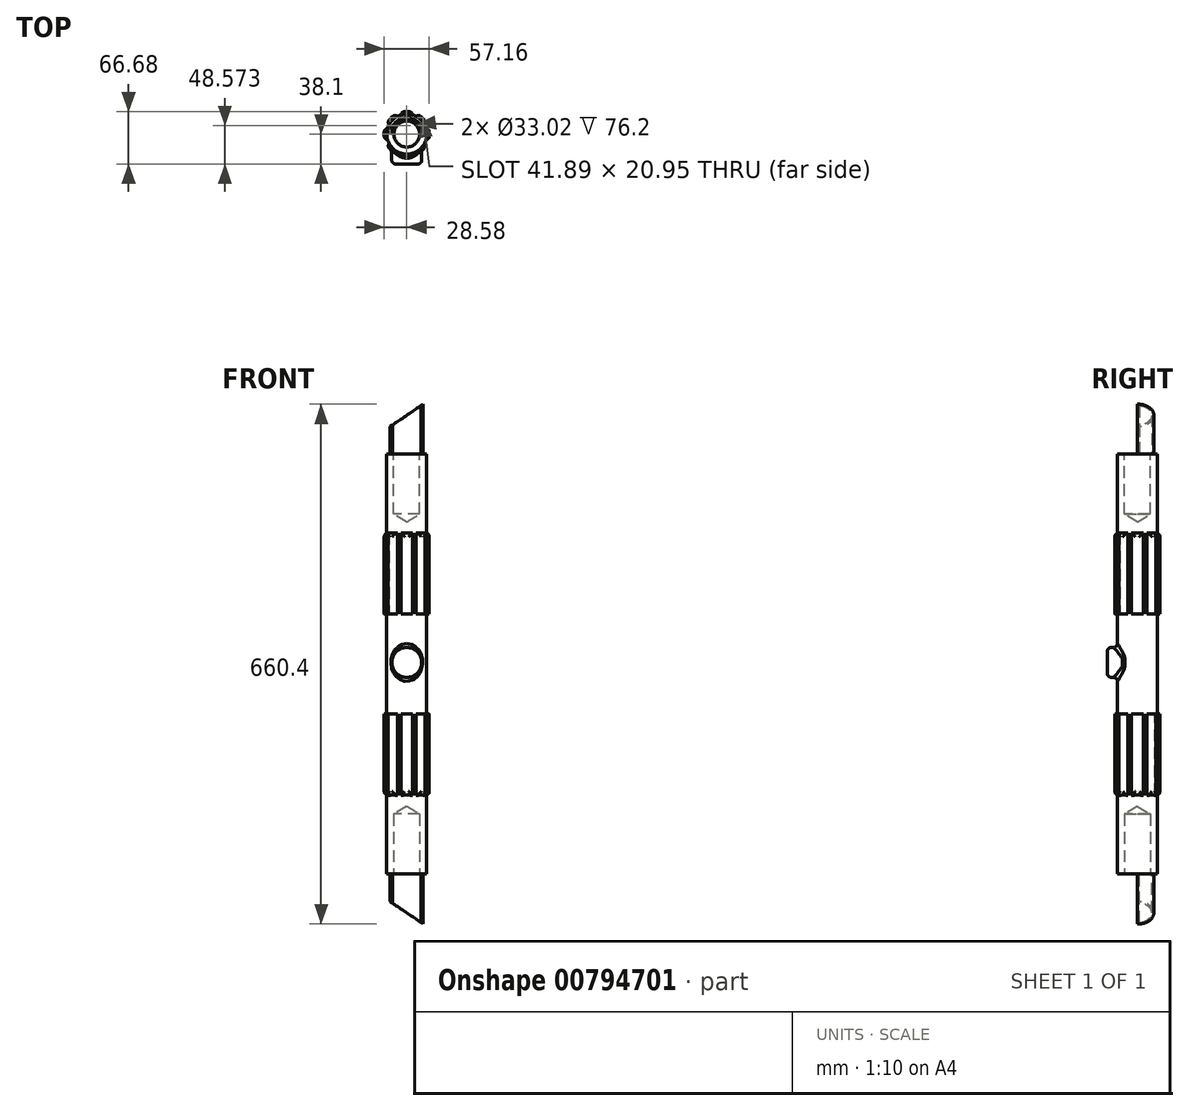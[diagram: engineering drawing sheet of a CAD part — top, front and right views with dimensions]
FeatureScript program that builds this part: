
annotation { "Feature Type Name" : "Feature", "Feature Type Description" : "" }
export const myFeature = defineFeature(function(context is Context, id is Id, definition is map)
    precondition{}
    {
        {
            var Q0;
            Q0=qCreatedBy(makeId("Top.planeOp"),FACE);
            var sketch = newSketch(context, id + "F0", { "sketchPlane" : qUnion([Q0])});
            skCircle(sketch, "E0", {"center": v(0, 0) * mm, "radius": 25.4 * mm});
            skSolve(sketch);
        }
        {
            var Q0;
            Q0 = qSketchRegion(id + "F0", true);
            extrude(context, id + "F1", {"entities" : qUnion([Q0]), "endBound" : BoundingType.SYMMETRIC, "depth" : 203.2 * mm, "offsetDistance" : 25.4 * mm});
        }
        {
            var Q0;
            Q0=makeQuery(id+"F1.opExtrude","CAP_FACE",FACE,{"disambiguationData":[OSD([sQuery(id+"F0.wireOp",EDGE,"E0")])],"isStart":false});
            var sketch = newSketch(context, id + "F2", { "sketchPlane" : qUnion([Q0])});
            skArc(sketch, "E1", {"start": v(20.95, 0) * mm, "mid": v(0, 20.95) * mm, "end": v(-20.95, 0) * mm});
            skArc(sketch, "E2.0", {"start": v(18.23, 2.54) * mm, "mid": v(0, 18.4) * mm, "end": v(-18.23, 2.54) * mm});
            skLineSegment(sketch, "E3", {"start": v(-18.23, 2.54) * mm, "end": v(-20.95, 0) * mm});
            skLineSegment(sketch, "E4", {"start": v(18.23, 2.54) * mm, "end": v(20.95, 0) * mm});
            skSolve(sketch);
        }
        {
            var Q0;
            Q0 = qSketchRegion(id + "F2", true);
            extrude(context, id + "F3", {"entities" : qUnion([Q0]), "operationType" : NewBodyOperationType.ADD, "depth" : 63.5 * mm, "offsetDistance" : 25.4 * mm});
        }
        {
            var Q0;
            Q0=qCreatedBy(makeId("Front.planeOp"),FACE);
            var sketch = newSketch(context, id + "F4", { "sketchPlane" : qUnion([Q0])});
            skLineSegment(sketch, "E5", {"start": v(21, 165.17) * mm, "end": v(-21.28, 136.4) * mm});
            skLineSegment(sketch, "E6", {"start": v(-21.28, 136.4) * mm, "end": v(-21.28, 165.82) * mm});
            skLineSegment(sketch, "E7", {"start": v(-21.28, 165.82) * mm, "end": v(21, 165.17) * mm});
            skSolve(sketch);
        }
        {
            var Q0;
            Q0 = qSketchRegion(id + "F4", true);
            extrude(context, id + "F5", {"entities" : qUnion([Q0]), "operationType" : NewBodyOperationType.REMOVE, "oppositeDirection" : true, "depth" : 25.4 * mm, "offsetDistance" : 25.4 * mm});
        }
        {
            var Q0;
            Q0=makeQuery(id+"F1.opExtrude","CAP_FACE",FACE,{"disambiguationData":[OSD([sQuery(id+"F0.wireOp",EDGE,"E0")])],"isStart":false});
            var sketch = newSketch(context, id + "F6", { "sketchPlane" : qUnion([Q0])});
            skPoint(sketch, "E8", {"position": v(0, 0) * mm});
            skSolve(sketch);
        }
        {
            var Q0;
            Q0=sQuery(id+"F6.wireOp",VERTEX,"E8");
            var Q1;
            Q1=makeQuery(id+"F1.opExtrude","SWEPT_BODY",BODY,{"disambiguationData":[OSD([sQuery(id+"F0.wireOp",EDGE,"E0")])]});
            hole(context, id + "F7", {"style" : HoleStyle.SIMPLE, "endStyle" : HoleEndStyle.BLIND, "holeDiameter" : 33.02 * mm, "majorDiameter" : 6.35 * mm, "holeDepth" : 76.2 * mm, "isTappedThrough" : true, "tappedDepth" : 12.7 * mm, "tapClearance" : 3, "locations" : qUnion([Q0]), "scope" : qUnion([Q1])});
        }
        {
            var Q0;
            Q0=qCreatedBy(makeId("Front.planeOp"),FACE);
            cPlane(context, id + "F8", {"entities" : qUnion([Q0]), "cplaneType" : CPlaneType.OFFSET, "offset" : 25.4 * mm, "width" : 152.4 * mm, "height" : 152.4 * mm});
        }
        {
            var Q0;
            Q0=qCreatedBy(id+"F8.planeOp",FACE);
            var sketch = newSketch(context, id + "F9", { "sketchPlane" : qUnion([Q0])});
            skLineSegment(sketch, "E9.bottom", {"start": v(7.6, 1.68) * mm, "end": v(-7.6, 1.68) * mm});
            skLineSegment(sketch, "E9.top", {"start": v(7.6, -101.6) * mm, "end": v(-7.6, -101.6) * mm});
            skLineSegment(sketch, "E9.left", {"start": v(7.6, 1.68) * mm, "end": v(7.6, -101.6) * mm});
            skLineSegment(sketch, "E9.right", {"start": v(-7.6, 1.68) * mm, "end": v(-7.6, -101.6) * mm});
            skPoint(sketch, "E9.middle", {"position": v(0, -49.96) * mm});
            skSolve(sketch);
        }
        {
            var Q0;
            Q0 = qSketchRegion(id + "F9", true);
            extrude(context, id + "F10", {"entities" : qUnion([Q0]), "endBound" : BoundingType.SYMMETRIC, "depth" : 6.35 * mm, "offsetDistance" : 25.4 * mm});
        }
        {
            var Q0;
            Q0=makeQuery(id+"F10.opExtrude","CAP_EDGE",EDGE,{"disambiguationData":[OSD([sQuery(id+"F9.wireOp",EDGE,"E9.right")])],"isStart":false});
            var Q1;
            Q1=makeQuery(id+"F10.opExtrude","CAP_EDGE",EDGE,{"disambiguationData":[OSD([sQuery(id+"F9.wireOp",EDGE,"E9.bottom")])],"isStart":false});
            var Q2;
            Q2=makeQuery(id+"F10.opExtrude","CAP_EDGE",EDGE,{"disambiguationData":[OSD([sQuery(id+"F9.wireOp",EDGE,"E9.left")])],"isStart":false});
            fillet(context, id + "F11", {"entities" : qUnion([Q0, Q1, Q2]), "radius" : 5.08 * mm, "tangentPropagation" : true, "allowEdgeOverflow" : false});
        }
        {
            var Q0;
            Q0=makeQuery(id+"F10.opExtrude","SWEPT_BODY",BODY,{"disambiguationData":[OSD([sQuery(id+"F9.wireOp",EDGE,"E9.bottom"),sQuery(id+"F9.wireOp",EDGE,"E9.top"),sQuery(id+"F9.wireOp",EDGE,"E9.left"),sQuery(id+"F9.wireOp",EDGE,"E9.right")])]});
            var Q1;
            Q1=makeQuery(id+"F1.opExtrude","SWEPT_FACE",FACE,{"disambiguationData":[OSD([sQuery(id+"F0.wireOp",EDGE,"E0")])]});
            circularPattern(context, id + "F12", {"entities" : qUnion([Q0]), "axis" : qUnion([Q1]), "angle" : 360 * degree, "instanceCount" : 8, "equalSpace" : true});
        }
        {
            var Q0;
            Q0=makeQuery(id+"F1.opExtrude","CAP_FACE",FACE,{"disambiguationData":[OSD([sQuery(id+"F0.wireOp",EDGE,"E0")])],"isStart":true});
            var sketch = newSketch(context, id + "F13", { "sketchPlane" : qUnion([Q0])});
            skCircle(sketch, "E10", {"center": v(0, 0) * mm, "radius": 25.4 * mm});
            skSolve(sketch);
        }
        {
            var Q0;
            Q0 = qSketchRegion(id + "F13", true);
            extrude(context, id + "F14", {"entities" : qUnion([Q0]), "operationType" : NewBodyOperationType.ADD, "depth" : 63.5 * mm, "offsetDistance" : 25.4 * mm});
        }
        {
            var Q0;
            Q0=makeQuery(id+"F1.opExtrude","SWEPT_BODY",BODY,{"disambiguationData":[OSD([sQuery(id+"F0.wireOp",EDGE,"E0")])]});
            var Q1;
            Q1=makeQuery(id+"F14.opExtrude","CAP_FACE",FACE,{"disambiguationData":[OSD([sQuery(id+"F13.wireOp",EDGE,"E10")])],"isStart":false});
            mirror(context, id + "F15", {"operationType" : NewBodyOperationType.ADD, "entities" : qUnion([Q0]), "mirrorPlane" : qUnion([Q1])});
        }
        {
            var Q0;
            Q0=qCreatedBy(makeId("Front.planeOp"),FACE);
            cPlane(context, id + "F16", {"entities" : qUnion([Q0]), "cplaneType" : CPlaneType.OFFSET, "offset" : 25.4 * mm, "width" : 152.4 * mm, "height" : 152.4 * mm});
        }
        {
            var Q0;
            Q0=qCreatedBy(id+"F16.planeOp",FACE);
            var sketch = newSketch(context, id + "F17", { "sketchPlane" : qUnion([Q0])});
            skCircle(sketch, "E11", {"center": v(0, -163) * mm, "radius": 19.05 * mm});
            skSolve(sketch);
        }
        {
            var Q0;
            Q0 = qSketchRegion(id + "F17", true);
            extrude(context, id + "F18", {"entities" : qUnion([Q0]), "operationType" : NewBodyOperationType.ADD, "endBound" : BoundingType.SYMMETRIC, "depth" : 25.4 * mm, "offsetDistance" : 25.4 * mm});
        }
        {
            var Q0;
            Q0=makeQuery(id+"F18.opExtrude","CAP_EDGE",EDGE,{"disambiguationData":[OSD([sQuery(id+"F17.wireOp",EDGE,"E11")])],"isStart":false});
            var Q1;
            {var subQ0=makeQuery(id+"F14.boolean.opBoolean","MERGE",FACE,{"derivedFrom":[makeQuery(id+"F1.opExtrude","SWEPT_FACE",FACE,{"disambiguationData":[OSD([sQuery(id+"F0.wireOp",EDGE,"E0")])]}),makeQuery(id+"F14.opExtrude","SWEPT_FACE",FACE,{"disambiguationData":[OSD([sQuery(id+"F13.wireOp",EDGE,"E10")])]})]});Q1=makeQuery(id+"F18.boolean.opBoolean","INTERSECT",EDGE,{"derivedFrom":[makeQuery(id+"F15.boolean.opBoolean","MERGE",FACE,{"derivedFrom":[subQ0,makeQuery(id+"F15.opPattern","COPY",FACE,{"derivedFrom":subQ0,"instanceName":"1"})]}),makeQuery(id+"F18.opExtrude","SWEPT_FACE",FACE,{"disambiguationData":[OSD([sQuery(id+"F17.wireOp",EDGE,"E11")])]})]});}
            fillet(context, id + "F19", {"entities" : qUnion([Q0, Q1]), "radius" : 5.08 * mm, "tangentPropagation" : true, "allowEdgeOverflow" : false});
        }
    });
